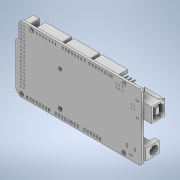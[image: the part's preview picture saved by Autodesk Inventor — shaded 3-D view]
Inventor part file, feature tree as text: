
AUTODESK INVENTOR PART (.ipt)
format: ipt  version: 2020 (Build 240168000, 168)  size: 1,251,840 bytes
history: native  units: in
note: dims shown in document units (in); Inventor stores cm internally (conversion verified against a paired STEP export)
features: sketch x1, fillet x1
ambient origin geometry x8: Origin, YZ Plane, XZ Plane, XY Plane, X Axis, Y Axis, Z Axis, Center Point
bodies: Solid1 (feature_tree)
feature tree (2):
  sketch  "Sketch1"
  fillet  "Fillet5"  [1 undecoded]
note: 1 required parameter value undecoded (feature->parameter linkage not recoverable at this tier; creation-order binding heuristic only, values carry confidence <= 0.55)
